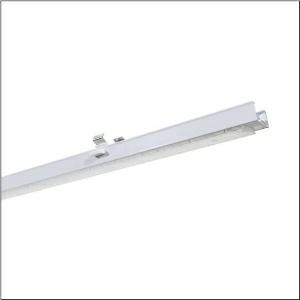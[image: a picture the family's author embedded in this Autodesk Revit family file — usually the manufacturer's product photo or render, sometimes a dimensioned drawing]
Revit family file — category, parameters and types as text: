
# Revit family: trunking_flex_31_51re11db49b
name_source: partatom
category: Lighting Fixtures
units: mm (PartAtom-declared; Revit-internal decimal feet)

## family parameters
Cut with Voids When Loaded = No
Host = Face
Light Source = No
Part Type = Normal
Room Calculation Point = No
Round Connector Dimension = Use Diameter
Shared = No

## types (1)
- Trunking Flex 31 (1 x LED, 8900 lm, 53 W, 4000K)
    Apparent Load = 53 VA
    CIE Flux Codes = 83 93 98 100 100
    Color Rendering = 80
    Color Temperature = 4000K
    Default Elevation = 1800 mm
    Description = Trunking Flex 31, luminaire insert, of extruded aluminium section, coated, traffic white (RAL 9016), length: 1.472mm, width: 91mm, height: 53mm, LED rated luminous flux: 8.900lm, light colour: 840, control gear: DALI 2, with system connector: socket, mains connection: 220..240V, AC, 50/60Hz, rated input power: 53W, primary light control with lens, of plastic, primary optical cover: cover, of PMMA, light emission: direct distribution, protection rating (complete): IP20, insulation class (complete): insulation class I (protective earthing), certification: CE, UKCA, impact resistance: IK02, permissible ambient temperature for indoor applications: -20..+40°C, packaging unit: 1 piece
    Height = 58 mm
    Lamp = 1 x LED
    Lamp Light Flux = 8900 lm
    Lamp Power = 53 W
    Lamp count = 1
    Length = 1472 mm
    Luminous efficacy = 168 lm/W
    Manufacturer = Siteco
    ModVariant = No
    Model = 51RE11DB49B
    Mounting Place = Ceiling
    Mounting Type = Pendant
    Number of Poles = 1
    OnlyDefault = Yes
    Power Factor = 1
    Product Name = Trunking Flex 31
    Product group = luminaire insert
    ProductGroupID = 902
    Protection Class = Protection class I
    Protection Degree = IP 20
    RLX_Detail_Level = 1
    RLX_Emergency_Light_Flux = 0 lm
    RLX_Emergency_Type = 0
    RLX_Emergency_Type_DB = No
    RlxData = <blob elided: 19433 chars, md5=ffb40615>
    Socket = socket
    Standby Power = 0 W
    System Light Flux = 8900 lm
    System Power = 53 W
    Type Comments = Product without accessories
    Type Image = l_1266702.jpg
    URL = http://relux.com
    VarID = ---
    Voltage = 0 V
    Weight = 0.00 kg
    Width = 65 mm

## geometry (parser evidence)
native form markers: Blend x4, Sweep x11
no freeform markers — native parametric forms only
